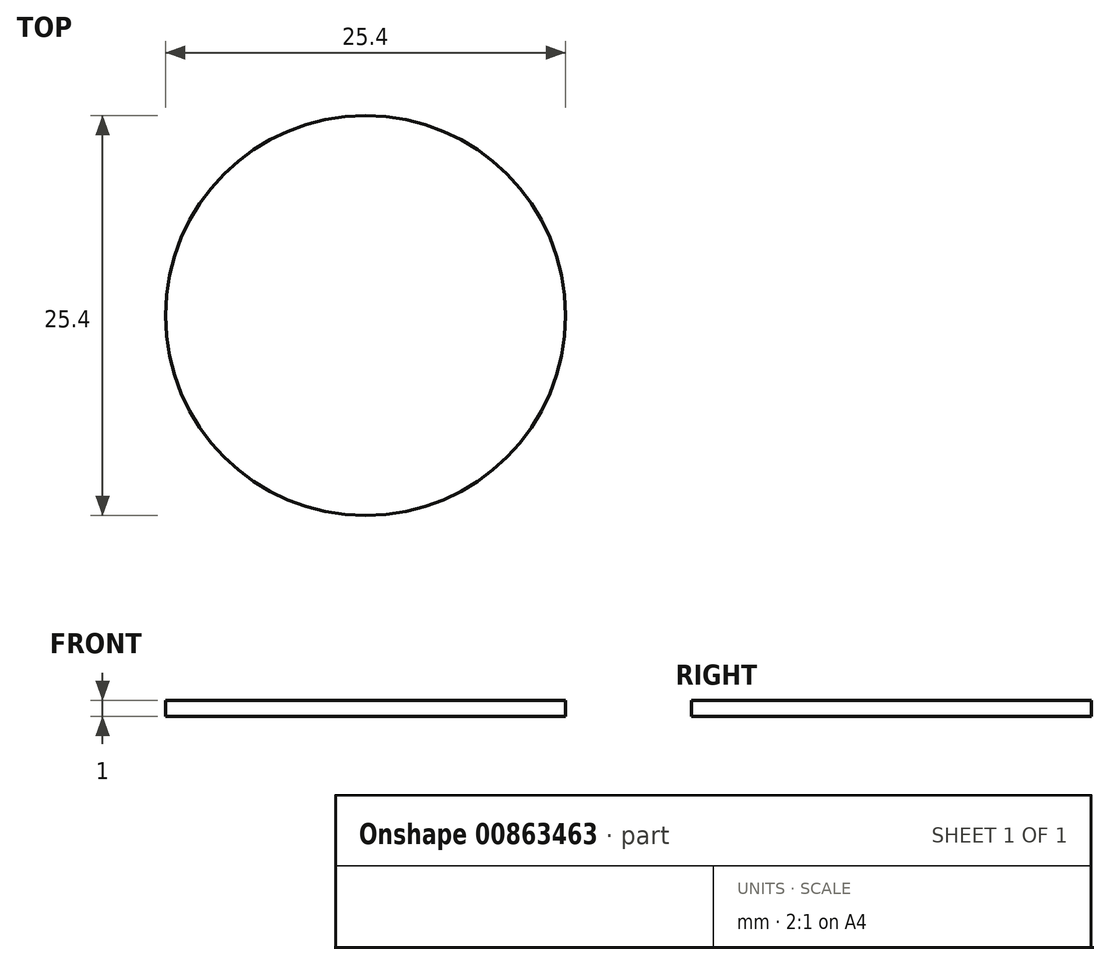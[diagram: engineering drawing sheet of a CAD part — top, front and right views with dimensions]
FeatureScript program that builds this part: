
annotation { "Feature Type Name" : "Feature", "Feature Type Description" : "" }
export const myFeature = defineFeature(function(context is Context, id is Id, definition is map)
    precondition{}
    {
        {
            var Q0;
            Q0=qCreatedBy(makeId("Top.planeOp"),FACE);
            var sketch = newSketch(context, id + "F0", { "sketchPlane" : qUnion([Q0])});
            skCircle(sketch, "E0", {"center": v(0, 0) * mm, "radius": 12.7 * mm});
            skCircle(sketch, "E1", {"center": v(0, 0) * mm, "radius": 9.53 * mm});
            skCircle(sketch, "E2", {"center": v(0, 0) * mm, "radius": 63.5 * mm});
            skSolve(sketch);
        }
        {
            assignVariable(context, id + "F1", {"name" : "hubHeight", "anyValue" : 1});
        }
        {
            var Q0;
            Q0=makeQuery(id+"F0.imprint","IMPRINT",FACE,{"disambiguationData":[TD([[makeQuery(id+"F0.imprint","IMPRINT",EDGE,{"derivedFrom":sQuery(id+"F0.wireOp",EDGE,"E0")}),1.0]])]});
            var Q1;
            Q1=makeQuery(id+"F0.imprint","IMPRINT",FACE,{"disambiguationData":[TD([[makeQuery(id+"F0.imprint","IMPRINT",EDGE,{"derivedFrom":sQuery(id+"F0.wireOp",EDGE,"E1")}),1.0]])]});
            extrude(context, id + "F2", {"entities" : qUnion([Q0, Q1]), "depth" : (getVariable(context, 'hubHeight')) * mm, "offsetDistance" : 25.4 * mm});
        }
    });
